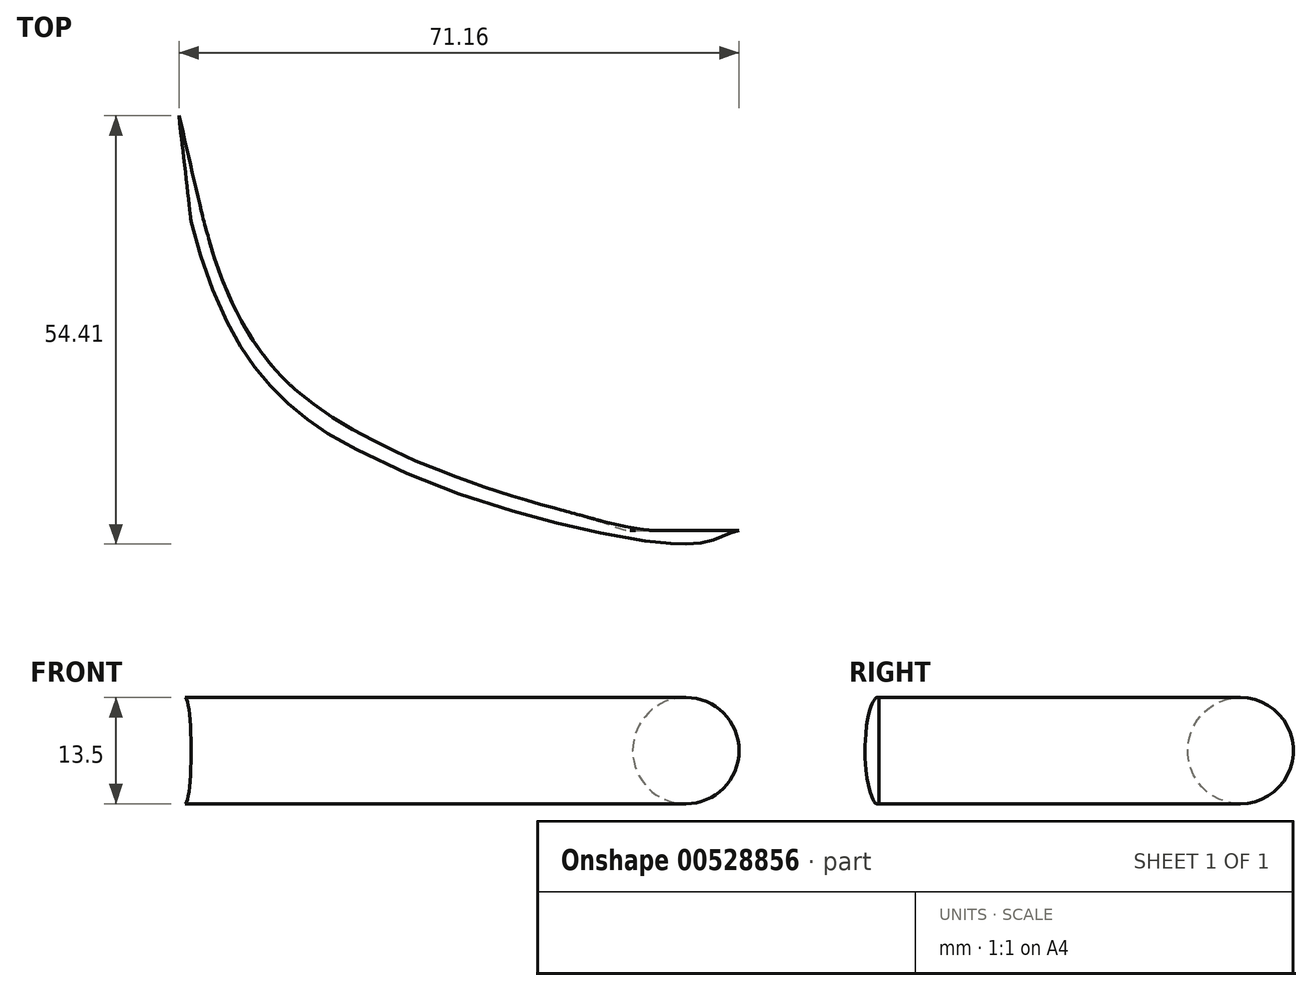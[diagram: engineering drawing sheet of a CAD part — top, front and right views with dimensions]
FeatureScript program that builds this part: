
annotation { "Feature Type Name" : "Feature", "Feature Type Description" : "" }
export const myFeature = defineFeature(function(context is Context, id is Id, definition is map)
    precondition{}
    {
        {
            var Q0;
            Q0=qCreatedBy(makeId("Front.planeOp"),FACE);
            var sketch = newSketch(context, id + "F0", { "sketchPlane" : qUnion([Q0])});
            skCircle(sketch, "E0", {"center": v(0, 0) * mm, "radius": 6.75 * mm});
            skSolve(sketch);
        }
        {
            var Q0;
            Q0=qCreatedBy(makeId("Top.planeOp"),FACE);
            var sketch = newSketch(context, id + "F1", { "sketchPlane" : qUnion([Q0])});
            skFitSpline(sketch, "E1", {"points": [v(0, 0) * mm, v(-6.34, 0) * mm, v(-47.83, 15.84) * mm, v(-63.63, 45.95) * mm], "startDerivative": vector(-27.2, -3.72) * mm, "endDerivative": vector(-21.83, 84.99) * mm});
            skSolve(sketch);
        }
        {
            var Q0;
            Q0 = qSketchRegion(id + "F0", true);
            var Q1;
            Q1 = qConstructionFilter(qBodyType(qCreatedBy(id + "F1" ,EDGE), BodyType.WIRE), ConstructionObject.NO);
            sweep(context, id + "F2", {"profiles" : qUnion([Q0]), "path" : qUnion([Q1])});
        }
    });
